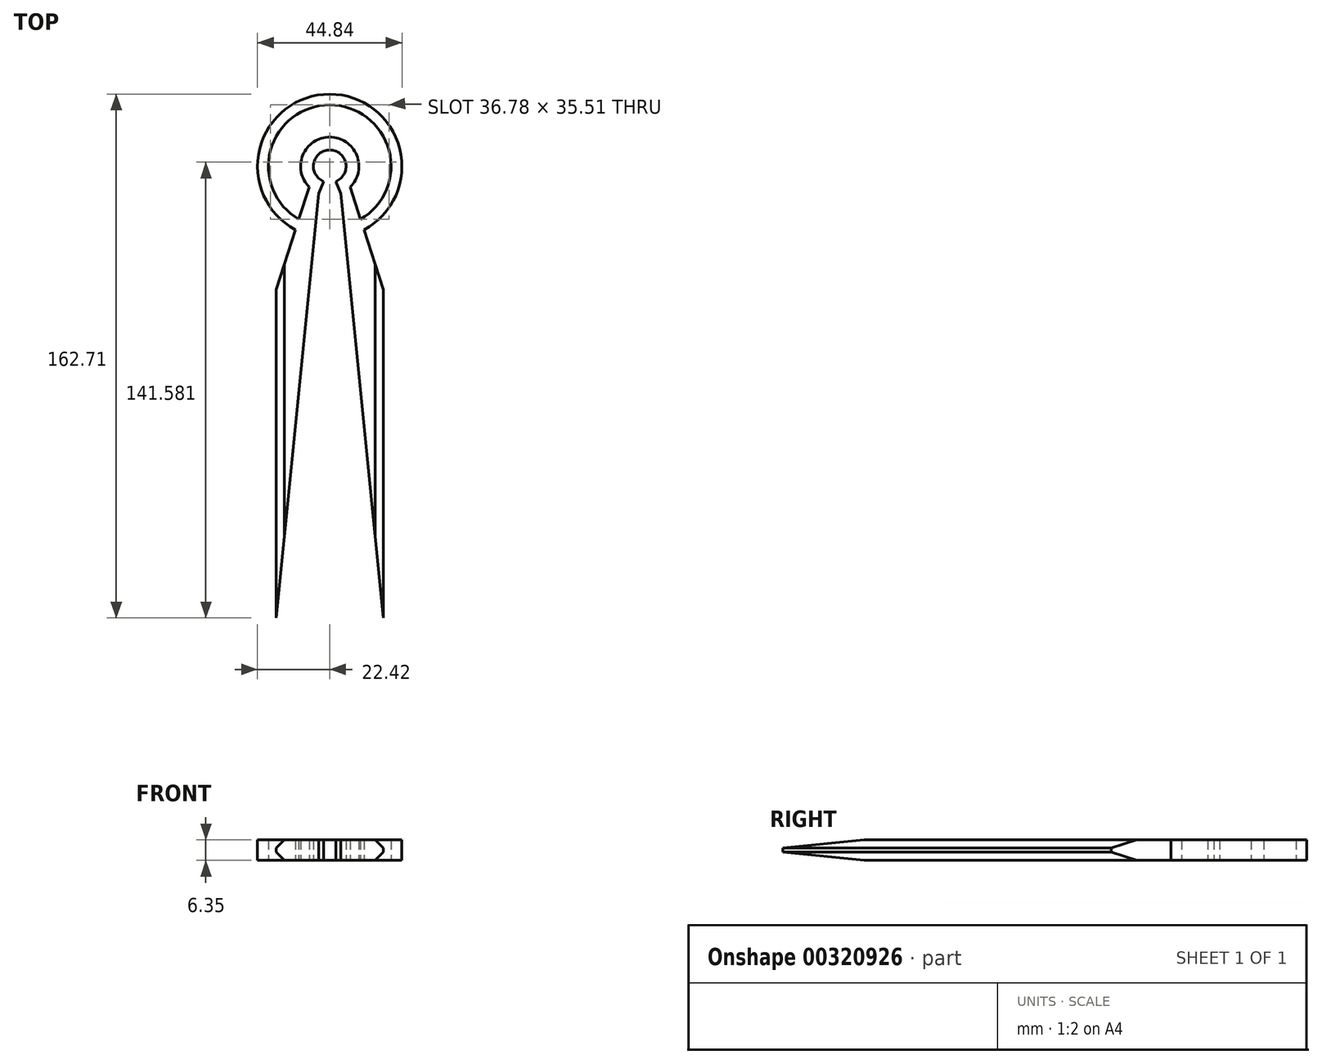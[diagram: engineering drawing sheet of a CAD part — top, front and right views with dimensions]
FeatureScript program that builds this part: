
annotation { "Feature Type Name" : "Feature", "Feature Type Description" : "" }
export const myFeature = defineFeature(function(context is Context, id is Id, definition is map)
    precondition{}
    {
        {
            var Q0;
            Q0=qCreatedBy(makeId("Top.planeOp"),FACE);
            var sketch = newSketch(context, id + "F0", { "sketchPlane" : qUnion([Q0])});
            skCircle(sketch, "E0", {"center": v(0, 43.12) * mm, "radius": 22.42 * mm});
            skCircle(sketch, "E1", {"center": v(0, 43.12) * mm, "radius": 9.05 * mm});
            skLineSegment(sketch, "E2", {"start": v(-3.38, 34.72) * mm, "end": v(-16.6, -97.17) * mm});
            skLineSegment(sketch, "E3", {"start": v(-16.6, -97.17) * mm, "end": v(-16.6, 4.81) * mm});
            skLineSegment(sketch, "E4", {"start": v(-16.6, 4.81) * mm, "end": v(-6.36, 36.68) * mm});
            skLineSegment(sketch, "E5.MirrorCS", {"start": v(3.38, 34.72) * mm, "end": v(16.6, -97.17) * mm});
            skLineSegment(sketch, "E6.MirrorCS", {"start": v(16.6, 4.81) * mm, "end": v(6.36, 36.68) * mm});
            skLineSegment(sketch, "E7.MirrorCS", {"start": v(16.6, -97.17) * mm, "end": v(16.6, 4.81) * mm});
            skPoint(sketch, "E8", {"position": v(-10.64, 23.38) * mm});
            skPoint(sketch, "E9", {"position": v(10.64, 23.38) * mm});
            skCircle(sketch, "E10", {"center": v(0, 43.12) * mm, "radius": 19.05 * mm});
            skCircle(sketch, "E11", {"center": v(0, 43.12) * mm, "radius": 5.08 * mm});
            skLineSegment(sketch, "E12", {"start": v(-3.38, 34.72) * mm, "end": v(0, 43.12) * mm});
            skLineSegment(sketch, "E13", {"start": v(3.38, 34.72) * mm, "end": v(0, 43.12) * mm});
            skSolve(sketch);
        }
        {
            var Q0;
            {var subQ5=sQuery(id+"F0.wireOp",EDGE,"E3");Q0=makeQuery(id+"F0.imprint","IMPRINT",FACE,{"disambiguationData":[TD([[makeQuery(id+"F0.imprint","IMPRINT",EDGE,{"derivedFrom":subQ5}),-1.0]])]});}
            var Q1;
            {var subQ5=sQuery(id+"F0.wireOp",EDGE,"E7.MirrorCS");Q1=makeQuery(id+"F0.imprint","IMPRINT",FACE,{"disambiguationData":[TD([[makeQuery(id+"F0.imprint","IMPRINT",EDGE,{"derivedFrom":subQ5}),1.0]])]});}
            var Q2;
            {var subQ0=sQuery(id+"F0.wireOp",EDGE,"E5.MirrorCS");var subQ1=sQuery(id+"F0.wireOp",EDGE,"E0");var subQ2=makeQuery(id+"F0.imprint","INTERSECT",VERTEX,{"derivedFrom":[subQ1,subQ0]});Q2=makeQuery(id+"F0.imprint","IMPRINT",FACE,{"disambiguationData":[TD([[makeQuery(id+"F0.imprint","IMPRINT",EDGE,{"disambiguationData":[TD([[subQ2,-1.0]])],"derivedFrom":subQ1}),1.0]])]});}
            var Q3;
            {var subQ1=sQuery(id+"F0.wireOp",EDGE,"E1");var subQ3=sQuery(id+"F0.wireOp",EDGE,"E6.MirrorCS");var subQ4=makeQuery(id+"F0.imprint","INTERSECT",VERTEX,{"derivedFrom":[subQ1,subQ3]});Q3=makeQuery(id+"F0.imprint","IMPRINT",FACE,{"disambiguationData":[TD([[makeQuery(id+"F0.imprint","IMPRINT",EDGE,{"disambiguationData":[TD([[subQ4,1.0]])],"derivedFrom":subQ3}),1.0]])]});}
            var Q4;
            {var subQ0=sQuery(id+"F0.wireOp",EDGE,"E2");var subQ1=sQuery(id+"F0.wireOp",EDGE,"E0");var subQ2=makeQuery(id+"F0.imprint","INTERSECT",VERTEX,{"derivedFrom":[subQ1,subQ0]});Q4=makeQuery(id+"F0.imprint","IMPRINT",FACE,{"disambiguationData":[TD([[makeQuery(id+"F0.imprint","IMPRINT",EDGE,{"disambiguationData":[TD([[subQ2,1.0]])],"derivedFrom":subQ1}),1.0]])]});}
            var Q5;
            {var subQ1=sQuery(id+"F0.wireOp",EDGE,"E1");var subQ3=sQuery(id+"F0.wireOp",EDGE,"E4");var subQ4=makeQuery(id+"F0.imprint","INTERSECT",VERTEX,{"derivedFrom":[subQ1,subQ3]});Q5=makeQuery(id+"F0.imprint","IMPRINT",FACE,{"disambiguationData":[TD([[makeQuery(id+"F0.imprint","IMPRINT",EDGE,{"disambiguationData":[TD([[subQ4,1.0]])],"derivedFrom":subQ3}),-1.0]])]});}
            var Q6;
            {var subQ0=sQuery(id+"F0.wireOp",EDGE,"E4");var subQ1=sQuery(id+"F0.wireOp",EDGE,"E0");var subQ2=makeQuery(id+"F0.imprint","INTERSECT",VERTEX,{"derivedFrom":[subQ1,subQ0]});Q6=makeQuery(id+"F0.imprint","IMPRINT",FACE,{"disambiguationData":[TD([[makeQuery(id+"F0.imprint","IMPRINT",EDGE,{"disambiguationData":[TD([[subQ2,1.0]])],"derivedFrom":subQ1}),1.0]])]});}
            var Q7;
            {var subQ5=sQuery(id+"F0.wireOp",EDGE,"E1");var subQ6=makeQuery(id+"F0.imprint","INTERSECT",VERTEX,{"derivedFrom":[subQ5,sQuery(id+"F0.wireOp",EDGE,"E4")]});Q7=makeQuery(id+"F0.imprint","IMPRINT",FACE,{"disambiguationData":[TD([[makeQuery(id+"F0.imprint","IMPRINT",EDGE,{"disambiguationData":[TD([[subQ6,1.0]])],"derivedFrom":subQ5}),1.0]])]});}
            extrude(context, id + "F1", {"entities" : qUnion([Q0, Q1, Q2, Q3, Q4, Q5, Q6, Q7]), "depth" : 6.35 * mm});
        }
        {
            var Q0;
            Q0=makeQuery(id+"F1.opExtrude","CAP_EDGE",EDGE,{"disambiguationData":[OSD([sQuery(id+"F0.wireOp",EDGE,"E3")])],"isStart":false});
            var Q1;
            Q1=makeQuery(id+"F1.opExtrude","CAP_EDGE",EDGE,{"disambiguationData":[OSD([sQuery(id+"F0.wireOp",EDGE,"E7.MirrorCS")])],"isStart":false});
            var Q2;
            Q2=makeQuery(id+"F1.opExtrude","CAP_EDGE",EDGE,{"disambiguationData":[OSD([sQuery(id+"F0.wireOp",EDGE,"E7.MirrorCS")])],"isStart":true});
            var Q3;
            Q3=makeQuery(id+"F1.opExtrude","CAP_EDGE",EDGE,{"disambiguationData":[OSD([sQuery(id+"F0.wireOp",EDGE,"E3")])],"isStart":true});
            chamfer(context, id + "F2", {"entities" : qUnion([Q0, Q1, Q2, Q3]), "width" : 2.54 * mm, "tangentPropagation" : true});
        }
    });
